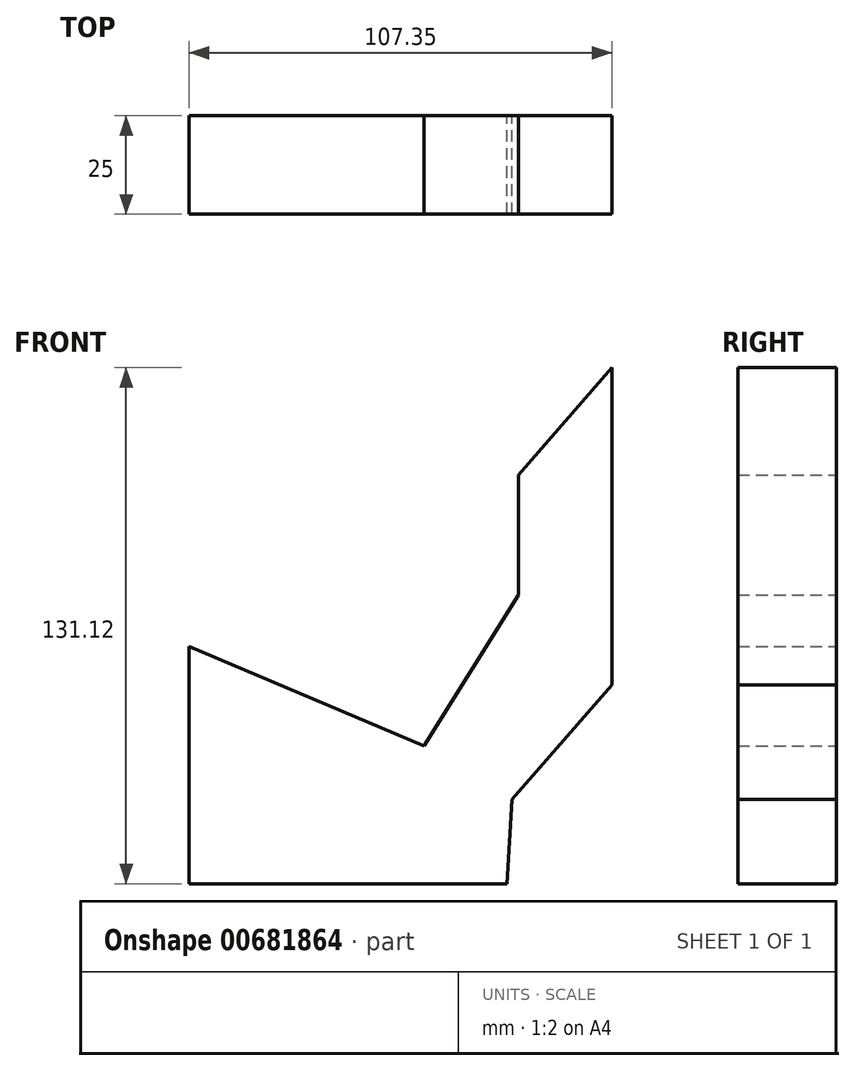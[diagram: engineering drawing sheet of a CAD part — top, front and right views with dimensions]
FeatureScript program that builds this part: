
annotation { "Feature Type Name" : "Feature", "Feature Type Description" : "" }
export const myFeature = defineFeature(function(context is Context, id is Id, definition is map)
    precondition{}
    {
        {
            var Q0;
            Q0=qCreatedBy(makeId("Front.planeOp"),FACE);
            var sketch = newSketch(context, id + "F0", { "sketchPlane" : qUnion([Q0])});
            skLineSegment(sketch, "E0", {"start": v(0, 0) * mm, "end": v(0, 60.3) * mm});
            skLineSegment(sketch, "E1", {"start": v(0, 60.3) * mm, "end": v(59.68, 34.96) * mm});
            skLineSegment(sketch, "E2", {"start": v(59.68, 34.96) * mm, "end": v(83.7, 73.4) * mm});
            skLineSegment(sketch, "E3", {"start": v(0, 0) * mm, "end": v(80.73, 0) * mm});
            skLineSegment(sketch, "E4", {"start": v(83.7, 73.4) * mm, "end": v(83.7, 103.9) * mm});
            skLineSegment(sketch, "E5", {"start": v(83.7, 103.9) * mm, "end": v(107.35, 131.12) * mm});
            skLineSegment(sketch, "E6", {"start": v(107.35, 131.12) * mm, "end": v(107.35, 50.51) * mm});
            skLineSegment(sketch, "E7", {"start": v(107.35, 50.51) * mm, "end": v(82.04, 21.4) * mm});
            skLineSegment(sketch, "E8", {"start": v(82.04, 21.4) * mm, "end": v(80.73, 0) * mm});
            skSolve(sketch);
        }
        {
            var Q0;
            Q0 = qSketchRegion(id + "F0", true);
            extrude(context, id + "F1", {"entities" : qUnion([Q0]), "depth" : 25 * mm, "offsetDistance" : 25 * mm});
        }
    });
